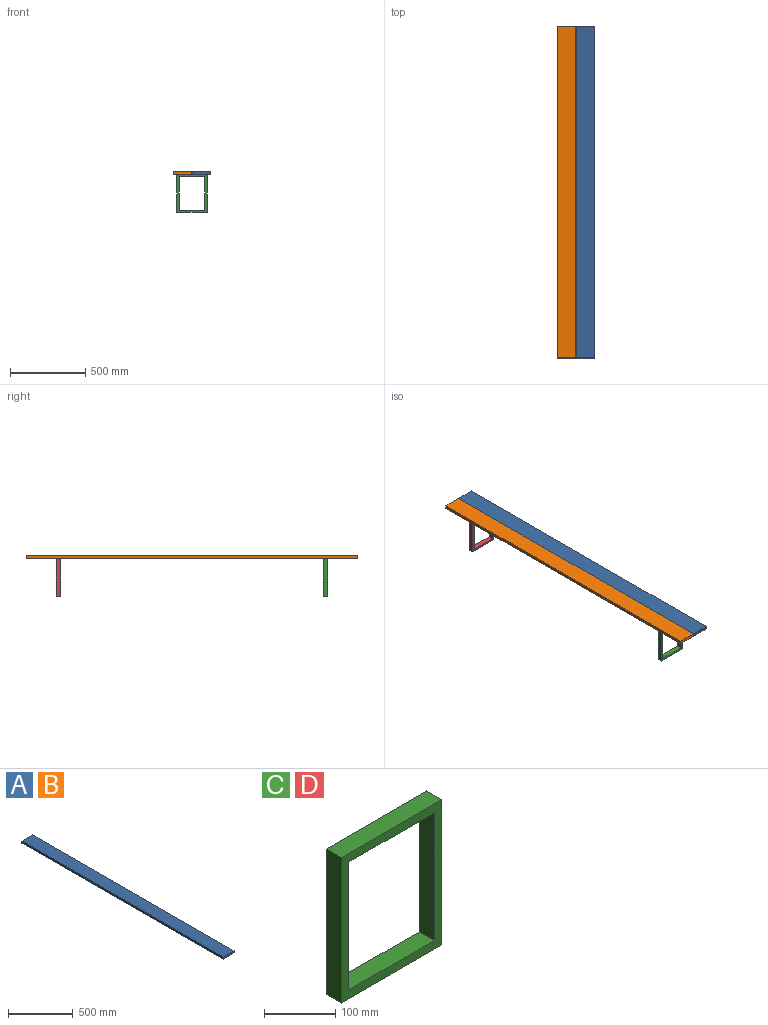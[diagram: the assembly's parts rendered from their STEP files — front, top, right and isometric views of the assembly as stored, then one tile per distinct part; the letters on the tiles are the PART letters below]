
ASSEMBLY  parts=4 mates=3
PART A: 6 faces, bbox 120x2200x20 mm
  f0: plane 2200x120mm, normal (0,0,1), area 264000mm2, adj f1,f3,f4,f5
  f1: plane 2200x20mm, normal (-1,0,0), area 44000mm2, adj f0,f2,f4,f5
  f2: plane 2200x120mm, normal (0,0,-1), area 264000mm2, adj f1,f3,f4,f5
  f3: plane 2200x20mm, normal (1,0,0), area 44000mm2, adj f0,f2,f4,f5
  f4: plane 120x20mm, normal (0,1,0), area 2400mm2, adj f0,f1,f2,f3
  f5: plane 120x20mm, normal (0,-1,0), area 2400mm2, adj f0,f1,f2,f3
PART B: same geometry as A
PART C: 10 faces, bbox 200x30x250 mm
  f0: plane 200x30mm, normal (0,0,1), area 6000mm2, adj f1,f7,f8,f9
  f1: plane 250x30mm, normal (-1,0,0), area 7500mm2, adj f0,f2,f8,f9
  f2: plane 200x30mm, normal (0,0,-1), area 6000mm2, adj f1,f7,f8,f9
  f3: plane 220x30mm, normal (-1,0,0), area 6600mm2, adj f4,f6,f8,f9
  f4: plane 170x30mm, normal (0,0,1), area 5100mm2, adj f3,f5,f8,f9
  f5: plane 220x30mm, normal (1,0,0), area 6600mm2, adj f4,f6,f8,f9
  f6: plane 170x30mm, normal (0,0,-1), area 5100mm2, adj f3,f5,f8,f9
  f7: plane 250x30mm, normal (1,0,0), area 7500mm2, adj f0,f2,f8,f9
  f8: plane 250x200mm, normal (0,1,0), area 12600mm2, adj f0,f1,f2,f3,f4,f5,f6,f7
  f9: plane 250x200mm, normal (0,-1,0), area 12600mm2, adj f0,f1,f2,f3,f4,f5,f6,f7
PART D: same geometry as C
PLACE A t=(1173.05,-844.38,-142.98)mm
PLACE B t=(1053.05,-844.38,-142.98)mm
PLACE C t=(1201.44,-644.38,-343.6)mm
PLACE D t=(1201.44,1125.62,-343.6)mm
MATE fastened D.f0 <-> B.f2  axis (0,0,1) through (622.64,1155.62,-335.54)mm
MATE fastened C.f0 <-> B.f2  axis (0,0,1) through (622.64,-644.38,-335.54)mm
MATE fastened B.f3 <-> A.f1  axis (1,0,0) through (722.64,-844.38,-315.54)mm
